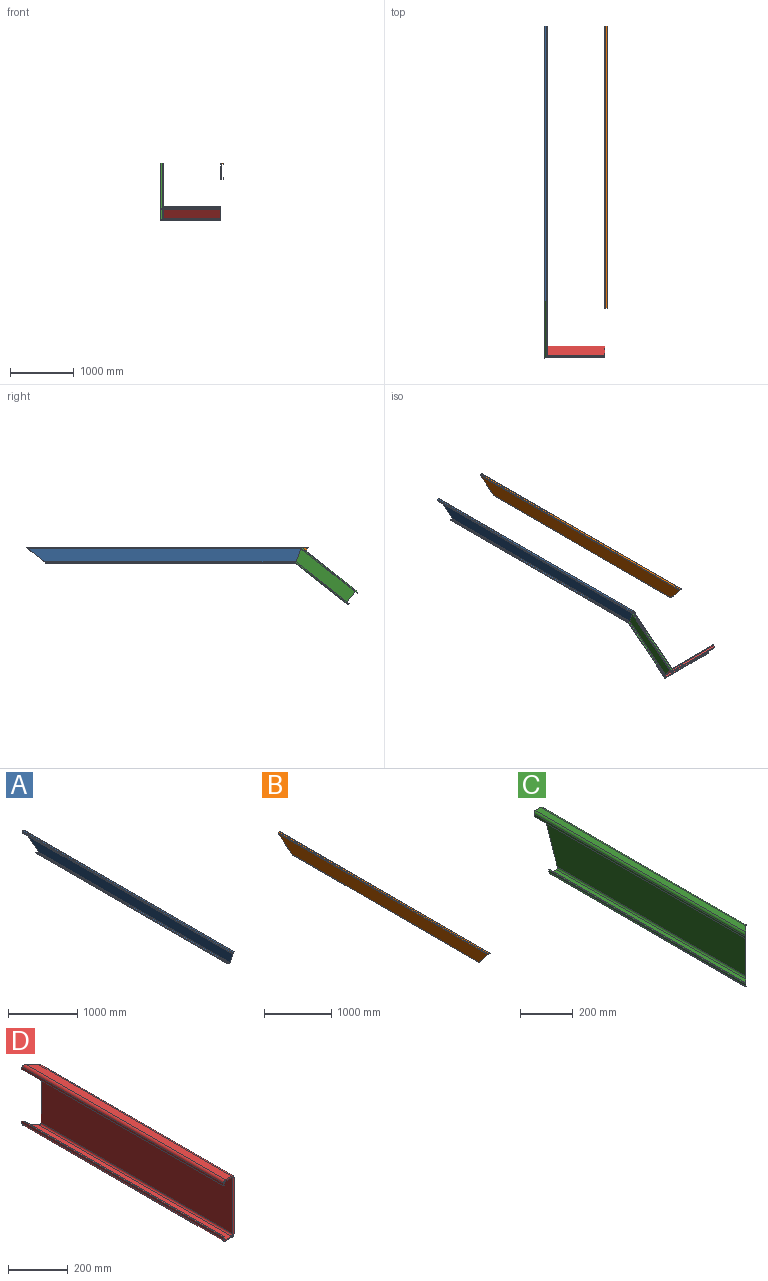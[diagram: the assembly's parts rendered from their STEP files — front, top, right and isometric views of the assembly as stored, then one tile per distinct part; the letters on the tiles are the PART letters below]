
ASSEMBLY  parts=4 mates=3
PART A: 22 faces, bbox 50x4299.8x250 mm
  f0: plane 4280.44x226mm, normal (-1,0,0), area 926235.5mm2, adj f12,f13,f20,f21
  f1: plane 3905.06x26mm, normal (0,0,1), area 101531.4mm2, adj f13,f14,f20,f21
  f2: plane 3929.22x8mm, normal (1,0,0), area 31382.2mm2, adj f3,f14,f20,f21
  f3: plane 3929.22x5mm, normal (0,0,1), area 19646.1mm2, adj f2,f4,f20,f21
  f4: plane 3929.22x10mm, normal (-1,0,0), area 39211.7mm2, adj f3,f15,f20,f21
  f5: plane 3897x30mm, normal (0,0,-1), area 116910mm2, adj f15,f16,f20,f21
  f6: plane 4283.66x230mm, normal (1,0,0), area 942629.1mm2, adj f16,f17,f20,f21
  f7: plane 4299.77x30mm, normal (0,0,1), area 128993.2mm2, adj f17,f18,f20,f21
  f8: plane 4283.66x10mm, normal (-1,0,0), area 42756.1mm2, adj f9,f18,f20,f21
  f9: plane 4267.55x5mm, normal (0,0,-1), area 21337.8mm2, adj f8,f10,f20,f21
  f10: plane 4280.44x8mm, normal (1,0,0), area 34192mm2, adj f9,f19,f20,f21
  f11: plane 4291.72x26mm, normal (0,0,-1), area 111584.7mm2, adj f12,f19,f20,f21
  f12: cylinder r=7mm len=4291.72mm, axis (0,1,0), area 47144.9mm2, adj f0,f11,f20,f21
  f13: cylinder r=7mm len=3916.33mm, axis (0,1,0), area 42983.4mm2, adj f0,f1,f20,f21
  f14: cylinder r=7mm len=3916.33mm, axis (0,1,0), area 42983.4mm2, adj f1,f2,f20,f21
  f15: cylinder r=10mm len=3913.11mm, axis (0,1,0), area 61305.9mm2, adj f4,f5,f20,f21
  f16: cylinder r=10mm len=3913.11mm, axis (0,1,0), area 61305.9mm2, adj f5,f6,f20,f21
  f17: cylinder r=10mm len=4299.77mm, axis (0,1,0), area 67448.7mm2, adj f6,f7,f20,f21
  f18: cylinder r=10mm len=4299.77mm, axis (0,1,0), area 67448.7mm2, adj f7,f8,f20,f21
  f19: cylinder r=7mm len=4291.72mm, axis (0,1,0), area 47144.9mm2, adj f10,f11,f20,f21
  f20: plane 315.8x250mm, normal (0,0.62,-0.78), area 2910mm2, adj f0,f1,f2,f3,f4,f5,f6,f7
  f21: plane 250x86.98mm, normal (0,-0.94,-0.33), area 1912.4mm2, adj f0,f1,f2,f3,f4,f5,f6,f7
PART B: 22 faces, bbox 50x4410.7x250 mm
  f0: plane 4386.05x226mm, normal (1,0,0), area 938771.4mm2, adj f12,f13,f20,f21
  f1: plane 3907.27x26mm, normal (0,0,1), area 101589.1mm2, adj f13,f14,f20,f21
  f2: plane 3938.1x8mm, normal (-1,0,0), area 31439mm2, adj f3,f14,f20,f21
  f3: plane 3938.1x5mm, normal (0,0,1), area 19690.5mm2, adj f2,f4,f20,f21
  f4: plane 3938.1x10mm, normal (1,0,0), area 39278.2mm2, adj f3,f15,f20,f21
  f5: plane 3897x30mm, normal (0,0,-1), area 116910mm2, adj f15,f16,f20,f21
  f6: plane 4390.16x230mm, normal (-1,0,0), area 955386.9mm2, adj f16,f17,f20,f21
  f7: plane 4410.71x30mm, normal (0,0,1), area 132321.4mm2, adj f17,f18,f20,f21
  f8: plane 4390.16x10mm, normal (1,0,0), area 43798.9mm2, adj f9,f18,f20,f21
  f9: plane 4369.62x5mm, normal (0,0,-1), area 21848.1mm2, adj f8,f10,f20,f21
  f10: plane 4386.05x8mm, normal (-1,0,0), area 35022.7mm2, adj f9,f19,f20,f21
  f11: plane 4400.44x26mm, normal (0,0,-1), area 114411.4mm2, adj f12,f19,f20,f21
  f12: cylinder r=7mm len=4400.44mm, axis (0,1,0), area 48327.9mm2, adj f0,f11,f20,f21
  f13: cylinder r=7mm len=3921.66mm, axis (0,1,0), area 43020.2mm2, adj f0,f1,f20,f21
  f14: cylinder r=7mm len=3921.66mm, axis (0,1,0), area 43020.2mm2, adj f1,f2,f20,f21
  f15: cylinder r=10mm len=3917.55mm, axis (0,1,0), area 61331.2mm2, adj f4,f5,f20,f21
  f16: cylinder r=10mm len=3917.55mm, axis (0,1,0), area 61331.2mm2, adj f5,f6,f20,f21
  f17: cylinder r=10mm len=4410.71mm, axis (0,1,0), area 69166mm2, adj f6,f7,f20,f21
  f18: cylinder r=10mm len=4410.71mm, axis (0,1,0), area 69166mm2, adj f7,f8,f20,f21
  f19: cylinder r=7mm len=4400.44mm, axis (0,1,0), area 48327.9mm2, adj f10,f11,f20,f21
  f20: plane 315.8x250mm, normal (0,0.62,-0.78), area 2910mm2, adj f0,f1,f2,f3,f4,f5,f6,f7
  f21: plane 250x197.92mm, normal (0,-0.78,-0.62), area 2303.7mm2, adj f0,f1,f2,f3,f4,f5,f6,f7
PART C: 22 faces, bbox 50x1137x250 mm
  f0: cylinder r=7mm len=1097.24mm, axis (0,1,0), area 12006.1mm2, adj f1,f19,f20,f21
  f1: plane 1087.8x226mm, normal (-1,0,0), area 236958.7mm2, adj f0,f2,f20,f21
  f2: cylinder r=7mm len=1016.18mm, axis (0,1,0), area 11107.4mm2, adj f1,f3,f20,f21
  f3: plane 1039.74x26mm, normal (0,0,1), area 26695.2mm2, adj f2,f4,f20,f21
  f4: cylinder r=7mm len=1049.18mm, axis (0,1,0), area 11491.3mm2, adj f3,f5,f20,f21
  f5: plane 1051.96x8mm, normal (1,0,0), area 8404.5mm2, adj f4,f6,f20,f21
  f6: plane 1056.96x5mm, normal (0,0,1), area 5272.3mm2, adj f5,f7,f20,f21
  f7: plane 1056.96x10mm, normal (-1,0,0), area 10552.2mm2, adj f6,f8,f20,f21
  f8: cylinder r=10mm len=1053.48mm, axis (0,1,0), area 16456.1mm2, adj f7,f9,f20,f21
  f9: plane 1040x30mm, normal (0,0,-1), area 30750mm2, adj f8,f10,f20,f21
  f10: cylinder r=10mm len=1013.48mm, axis (0,1,0), area 15784.9mm2, adj f9,f11,f20,f21
  f11: plane 1083.5x230mm, normal (1,0,0), area 240002.7mm2, adj f10,f12,f20,f21
  f12: cylinder r=10mm len=1096.98mm, axis (0,1,0), area 17111.5mm2, adj f11,f13,f20,f21
  f13: plane 1126.98x30mm, normal (0,0,1), area 33359.4mm2, adj f12,f14,f20,f21
  f14: cylinder r=10mm len=1136.98mm, axis (0,1,0), area 17782.7mm2, adj f13,f15,f20,f21
  f15: plane 1133.5x10mm, normal (-1,0,0), area 11317.6mm2, adj f14,f16,f20,f21
  f16: plane 1130.02x5mm, normal (0,0,-1), area 5637.6mm2, adj f15,f17,f20,f21
  f17: plane 1127.8x8mm, normal (1,0,0), area 9011.3mm2, adj f16,f18,f20,f21
  f18: cylinder r=7mm len=1130.24mm, axis (0,1,0), area 12389.9mm2, adj f17,f19,f20,f21
  f19: plane 1123.24x26mm, normal (0,0,-1), area 28866.2mm2, adj f0,f18,f20,f21
  f20: plane 250x50mm, normal (0.71,-0.71,0), area 2554.4mm2, adj f0,f1,f2,f3,f4,f5,f6,f7
  f21: plane 250x86.98mm, normal (0,0.94,-0.33), area 1912.4mm2, adj f0,f1,f2,f3,f4,f5,f6,f7
PART D: 22 faces, bbox 50x950x250 mm
  f0: plane 938x26mm, normal (0,0,-1), area 24050mm2, adj f1,f19,f20,f21
  f1: cylinder r=7mm len=945mm, axis (0,1,0), area 10362.8mm2, adj f0,f2,f20,f21
  f2: plane 945x8mm, normal (1,0,0), area 7560mm2, adj f1,f3,f20,f21
  f3: plane 950x5mm, normal (0,0,-1), area 4737.5mm2, adj f2,f4,f20,f21
  f4: plane 950x10mm, normal (-1,0,0), area 9500mm2, adj f3,f5,f20,f21
  f5: cylinder r=10mm len=950mm, axis (0,1,0), area 14865.5mm2, adj f4,f6,f20,f21
  f6: plane 940x30mm, normal (0,0,1), area 27750mm2, adj f5,f7,f20,f21
  f7: cylinder r=10mm len=910mm, axis (0,1,0), area 14194.2mm2, adj f6,f8,f20,f21
  f8: plane 900x230mm, normal (1,0,0), area 207000mm2, adj f7,f9,f20,f21
  f9: cylinder r=10mm len=910mm, axis (0,1,0), area 14194.2mm2, adj f8,f10,f20,f21
  f10: plane 940x30mm, normal (0,0,-1), area 27750mm2, adj f9,f11,f20,f21
  f11: cylinder r=10mm len=950mm, axis (0,1,0), area 14865.5mm2, adj f10,f12,f20,f21
  f12: plane 950x10mm, normal (-1,0,0), area 9500mm2, adj f11,f13,f20,f21
  f13: plane 950x5mm, normal (0,0,1), area 4737.5mm2, adj f12,f14,f20,f21
  f14: plane 945x8mm, normal (1,0,0), area 7560mm2, adj f13,f15,f20,f21
  f15: cylinder r=7mm len=945mm, axis (0,1,0), area 10362.8mm2, adj f14,f16,f20,f21
  f16: plane 938x26mm, normal (0,0,1), area 24050mm2, adj f15,f17,f20,f21
  f17: cylinder r=7mm len=912mm, axis (0,1,0), area 9979mm2, adj f16,f18,f20,f21
  f18: plane 905x226mm, normal (-1,0,0), area 204530mm2, adj f17,f19,f20,f21
  f19: cylinder r=7mm len=912mm, axis (0,1,0), area 9979mm2, adj f0,f18,f20,f21
  f20: plane 250x50mm, normal (0.71,0.71,0), area 2554.4mm2, adj f0,f1,f2,f3,f4,f5,f6,f7
  f21: plane 250x50mm, normal (0,-1,0), area 1806.2mm2, adj f0,f1,f2,f3,f4,f5,f6,f7
PLACE A t=(-1955.07,397.82,-786.78)mm
PLACE B t=(-1955.07,397.82,-786.78)mm
PLACE C rot(axis=(1,0,0),38.4deg) t=(-1933.28,-3576.76,-688.77)mm
PLACE D rot(axis=(0.31,-0.31,0.9),96.2deg) t=(-2055.07,-4382.93,-1326.99)mm
MATE fastened B.f20 <-> A.f20  axis (0,0.62,-0.78) through (-1005.07,555.72,-661.78)mm
MATE fastened D.f20 <-> C.f20  axis (-0.71,0.55,0.44) through (-1930.07,-4458,-1226.99)mm
MATE fastened C.f21 <-> A.f21  axis (0,0.94,0.33) through (-1905.07,-3542.67,-661.78)mm
